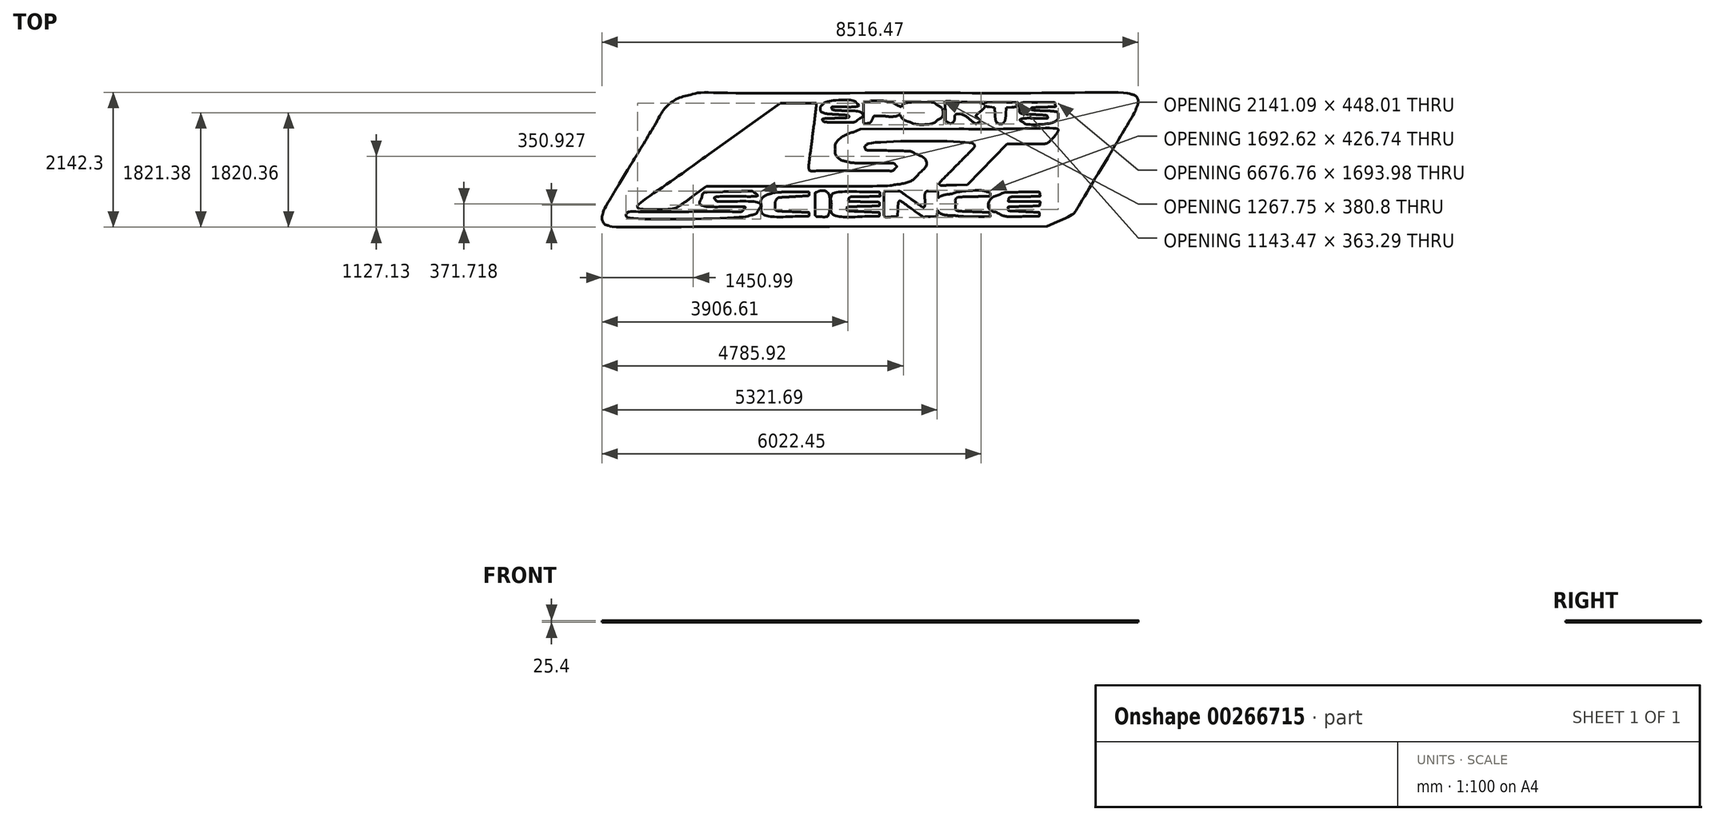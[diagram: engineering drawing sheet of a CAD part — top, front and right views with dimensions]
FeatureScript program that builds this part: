
annotation { "Feature Type Name" : "Feature", "Feature Type Description" : "" }
export const myFeature = defineFeature(function(context is Context, id is Id, definition is map)
    precondition{}
    {
        {
            var Q0;
            Q0=qCreatedBy(makeId("Top.planeOp"),FACE);
            var sketch = newSketch(context, id + "F0", { "sketchPlane" : qUnion([Q0])});
            skFitSpline(sketch, "E0", {"points": [v(-4148.25, -1047.03) * mm, v(-4215.36, -1022.28) * mm, v(-4255.3, -931.26) * mm, v(-4236.55, -845.83) * mm]});
            skFitSpline(sketch, "E1", {"points": [v(-4236.55, -845.83) * mm, v(-4228.8, -810.56) * mm, v(-4052.96, -501.34) * mm, v(-3845.8, -158.69) * mm]});
            skFitSpline(sketch, "E2", {"points": [v(-3845.8, -158.69) * mm, v(-3638.63, 183.97) * mm, v(-3431.5, 527.13) * mm, v(-3385.53, 603.9) * mm]});
            skFitSpline(sketch, "E3", {"points": [v(-3385.53, 603.9) * mm, v(-3262.4, 809.52) * mm, v(-3062.75, 967.71) * mm, v(-2846.13, 1031.34) * mm]});
            skFitSpline(sketch, "E4", {"points": [v(-2846.13, 1031.34) * mm, v(-2747.02, 1060.45) * mm, v(-2388.03, 1063.76) * mm, v(671.28, 1063.76) * mm]});
            skFitSpline(sketch, "E5", {"points": [v(671.28, 1063.76) * mm, v(3028.67, 1063.76) * mm, v(4097.44, 1057.1) * mm, v(4140.4, 1042.12) * mm]});
            skFitSpline(sketch, "E6", {"points": [v(4140.4, 1042.12) * mm, v(4224.04, 1012.96) * mm, v(4260.96, 924.63) * mm, v(4230.7, 826.04) * mm]});
            skFitSpline(sketch, "E7", {"points": [v(4230.7, 826.04) * mm, v(4218.45, 786.14) * mm, v(4013.65, 428.8) * mm, v(3775.57, 31.96) * mm]});
            skFitSpline(sketch, "E8", {"points": [v(3775.57, 31.96) * mm, v(3285.7, -784.61) * mm, v(3221.97, -865.04) * mm, v(2969.12, -985.79) * mm]});
            skFitSpline(sketch, "E9", {"points": [v(-640.01, -1063.28) * mm, v(-2847.05, -1065.57) * mm, v(-4113.85, -1059.7) * mm, v(-4148.25, -1047.03) * mm]});
            skLineSegment(sketch, "E10", {"start": v(2969.12, -985.79) * mm, "end": v(2814.39, -1059.68) * mm});
            skLineSegment(sketch, "E11", {"start": v(2814.39, -1059.68) * mm, "end": v(-640.01, -1063.28) * mm});
            skFitSpline(sketch, "E12", {"points": [v(-1909.68, -885) * mm, v(-1831.18, -868.16) * mm, v(-1800.22, -850.57) * mm, v(-1783.16, -813.12) * mm]});
            skFitSpline(sketch, "E13", {"points": [v(-1783.16, -813.12) * mm, v(-1735.07, -707.58) * mm, v(-1857.4, -664.67) * mm, v(-2208.53, -663.93) * mm]});
            skFitSpline(sketch, "E14", {"points": [v(-2208.53, -663.93) * mm, v(-2337.95, -663.65) * mm, v(-2441.36, -654.67) * mm, v(-2448.52, -643.08) * mm]});
            skFitSpline(sketch, "E15", {"points": [v(-2448.52, -643.08) * mm, v(-2473.2, -603.16) * mm, v(-2350.55, -582.16) * mm, v(-2092.77, -582.16) * mm]});
            skFitSpline(sketch, "E16", {"points": [v(-2092.77, -582.16) * mm, v(-1834, -582.16) * mm, v(-1780.77, -569.44) * mm, v(-1838.6, -521.44) * mm]});
            skFitSpline(sketch, "E17", {"points": [v(-1838.6, -521.44) * mm, v(-1860.25, -503.47) * mm, v(-1961.02, -499.03) * mm, v(-2209.22, -505.1) * mm]});
            skFitSpline(sketch, "E18", {"points": [v(-2209.22, -505.1) * mm, v(-2565.37, -513.82) * mm, v(-2649.73, -532.26) * mm, v(-2673.3, -606.54) * mm]});
            skFitSpline(sketch, "E19", {"points": [v(-2673.3, -606.54) * mm, v(-2703.6, -701.99) * mm, v(-2580.3, -744.45) * mm, v(-2272.36, -744.6) * mm]});
            skFitSpline(sketch, "E20", {"points": [v(-2272.36, -744.6) * mm, v(-2027.25, -744.74) * mm, v(-1977.9, -754.9) * mm, v(-2013.58, -797.9) * mm]});
            skFitSpline(sketch, "E21", {"points": [v(-2013.58, -797.9) * mm, v(-2032.8, -821.05) * mm, v(-2195.36, -826) * mm, v(-2936.17, -826) * mm]});
            skFitSpline(sketch, "E22", {"points": [v(-2936.17, -826) * mm, v(-3663.68, -826) * mm, v(-3839.76, -831.2) * mm, v(-3858.07, -853.27) * mm]});
            skFitSpline(sketch, "E23", {"points": [v(-3858.07, -853.27) * mm, v(-3870.52, -868.27) * mm, v(-3874.69, -886.56) * mm, v(-3867.33, -893.91) * mm]});
            skFitSpline(sketch, "E24", {"points": [v(-3867.33, -893.91) * mm, v(-3843.7, -917.53) * mm, v(-2022.73, -909.24) * mm, v(-1909.68, -885) * mm]});
            skFitSpline(sketch, "E25", {"points": [v(-965.13, -866.64) * mm, v(-965.13, -841.88) * mm, v(-1009.38, -834.25) * mm, v(-1200.82, -826) * mm]});
            skFitSpline(sketch, "E26", {"points": [v(-1200.82, -826) * mm, v(-1452.9, -815.13) * mm, v(-1503.61, -796.24) * mm, v(-1503.61, -713.2) * mm]});
            skFitSpline(sketch, "E27", {"points": [v(-1503.61, -713.2) * mm, v(-1503.61, -670.41) * mm, v(-1459.61, -606.2) * mm, v(-1425.96, -599.9) * mm]});
            skFitSpline(sketch, "E28", {"points": [v(-1425.96, -599.9) * mm, v(-1418.38, -598.47) * mm, v(-1311.6, -591.62) * mm, v(-1188.65, -584.66) * mm]});
            skFitSpline(sketch, "E29", {"points": [v(-1188.65, -584.66) * mm, v(-1009.14, -574.5) * mm, v(-965.13, -566) * mm, v(-965.13, -541.52) * mm]});
            skFitSpline(sketch, "E30", {"points": [v(-965.13, -541.52) * mm, v(-965.13, -515.92) * mm, v(-1007.44, -511.26) * mm, v(-1229.3, -512.38) * mm]});
            skFitSpline(sketch, "E31", {"points": [v(-1229.3, -512.38) * mm, v(-1378.73, -513.14) * mm, v(-1525.25, -524.43) * mm, v(-1566.67, -538.37) * mm]});
            skFitSpline(sketch, "E32", {"points": [v(-1566.67, -538.37) * mm, v(-1673.12, -574.21) * mm, v(-1731.48, -644.13) * mm, v(-1723.5, -726.27) * mm]});
            skFitSpline(sketch, "E33", {"points": [v(-1723.5, -726.27) * mm, v(-1711.16, -853.4) * mm, v(-1551.25, -905.43) * mm, v(-1188.65, -900.29) * mm]});
            skFitSpline(sketch, "E34", {"points": [v(-1188.65, -900.29) * mm, v(-1004.92, -897.68) * mm, v(-965.13, -891.7) * mm, v(-965.13, -866.64) * mm]});
            skFitSpline(sketch, "E35", {"points": [v(-662.5, -875.14) * mm, v(-640.03, -816.56) * mm, v(-649.19, -550.64) * mm, v(-674.56, -525.27) * mm]});
            skFitSpline(sketch, "E36", {"points": [v(-674.56, -525.27) * mm, v(-700.59, -499.24) * mm, v(-788.58, -492.89) * mm, v(-841.55, -513.22) * mm]});
            skFitSpline(sketch, "E37", {"points": [v(-841.55, -513.22) * mm, v(-867.46, -523.16) * mm, v(-873.7, -559.92) * mm, v(-873.7, -702.87) * mm]});
            skFitSpline(sketch, "E38", {"points": [v(-873.7, -702.87) * mm, v(-873.7, -800.4) * mm, v(-867.6, -886.28) * mm, v(-860.15, -893.73) * mm]});
            skFitSpline(sketch, "E39", {"points": [v(-860.15, -893.73) * mm, v(-852.7, -901.19) * mm, v(-807.96, -907.28) * mm, v(-760.72, -907.28) * mm]});
            skFitSpline(sketch, "E40", {"points": [v(-760.72, -907.28) * mm, v(-701.16, -907.28) * mm, v(-671.06, -897.43) * mm, v(-662.5, -875.14) * mm]});
            skFitSpline(sketch, "E41", {"points": [v(152.47, -866.64) * mm, v(152.47, -841.9) * mm, v(108.44, -834.25) * mm, v(-81.21, -826) * mm]});
            skFitSpline(sketch, "E42", {"points": [v(-81.21, -826) * mm, v(-307.16, -816.18) * mm, v(-365.7, -803.51) * mm, v(-365.7, -764.45) * mm]});
            skFitSpline(sketch, "E43", {"points": [v(-365.7, -764.45) * mm, v(-365.7, -754.27) * mm, v(-249.1, -743.38) * mm, v(-106.61, -740.25) * mm]});
            skFitSpline(sketch, "E44", {"points": [v(-106.61, -740.25) * mm, v(107.6, -735.55) * mm, v(152.47, -729.28) * mm, v(152.47, -704.08) * mm]});
            skFitSpline(sketch, "E45", {"points": [v(152.47, -704.08) * mm, v(152.47, -678.95) * mm, v(108.56, -672.6) * mm, v(-97.94, -667.88) * mm]});
            skFitSpline(sketch, "E46", {"points": [v(-97.94, -667.88) * mm, v(-280.57, -663.71) * mm, v(-346.15, -655.62) * mm, v(-340.27, -637.96) * mm]});
            skFitSpline(sketch, "E47", {"points": [v(-340.27, -637.96) * mm, v(-327.63, -600.06) * mm, v(-249.7, -586.38) * mm, v(-34, -584.19) * mm]});
            skFitSpline(sketch, "E48", {"points": [v(-34, -584.19) * mm, v(144.6, -582.37) * mm, v(164.88, -578.42) * mm, v(158.68, -546.6) * mm]});
            skFitSpline(sketch, "E49", {"points": [v(158.68, -546.6) * mm, v(152.56, -515.2) * mm, v(124.48, -511.05) * mm, v(-81.57, -511.1) * mm]});
            skFitSpline(sketch, "E50", {"points": [v(-81.57, -511.1) * mm, v(-484.03, -511.2) * mm, v(-609.53, -558.93) * mm, v(-609.53, -711.89) * mm]});
            skFitSpline(sketch, "E51", {"points": [v(-609.53, -711.89) * mm, v(-609.53, -850.23) * mm, v(-454.7, -905.46) * mm, v(-81.21, -900.33) * mm]});
            skFitSpline(sketch, "E52", {"points": [v(-81.21, -900.33) * mm, v(111.53, -897.68) * mm, v(152.47, -891.78) * mm, v(152.47, -866.64) * mm]});
            skFitSpline(sketch, "E53", {"points": [v(443.19, -785.36) * mm, v(446.62, -723.9) * mm, v(455.77, -667.35) * mm, v(463.5, -659.7) * mm]});
            skFitSpline(sketch, "E54", {"points": [v(463.5, -659.7) * mm, v(471.25, -652.06) * mm, v(559.88, -704.89) * mm, v(660.47, -777.1) * mm]});
            skFitSpline(sketch, "E55", {"points": [v(660.47, -777.1) * mm, v(838, -904.56) * mm, v(846.6, -908.23) * mm, v(955.1, -902.76) * mm]});
            skFitSpline(sketch, "E56", {"points": [v(1072.79, -715.96) * mm, v(1079.15, -521.13) * mm, v(1070.28, -501.77) * mm, v(974.4, -501.2) * mm]});
            skFitSpline(sketch, "E57", {"points": [v(974.4, -501.2) * mm, v(899.17, -500.74) * mm, v(873.83, -537.22) * mm, v(873.83, -645.99) * mm]});
            skFitSpline(sketch, "E58", {"points": [v(873.83, -645.99) * mm, v(873.83, -698.97) * mm, v(866.97, -746.44) * mm, v(858.59, -751.48) * mm]});
            skFitSpline(sketch, "E59", {"points": [v(858.59, -751.48) * mm, v(850.2, -756.51) * mm, v(761.96, -702.19) * mm, v(662.48, -630.76) * mm]});
            skFitSpline(sketch, "E60", {"points": [v(662.48, -630.76) * mm, v(494.48, -510.12) * mm, v(473.93, -500.88) * mm, v(373.63, -500.88) * mm]});
            skFitSpline(sketch, "E61", {"points": [v(373.63, -500.88) * mm, v(240.2, -500.88) * mm, v(223.59, -525.03) * mm, v(223.59, -719) * mm]});
            skFitSpline(sketch, "E62", {"points": [v(223.59, -719) * mm, v(223.59, -883.72) * mm, v(243.43, -911.4) * mm, v(355.57, -903.13) * mm]});
            skLineSegment(sketch, "E63", {"start": v(955.1, -902.76) * mm, "end": v(1066.87, -897.12) * mm});
            skLineSegment(sketch, "E64", {"start": v(1066.87, -897.12) * mm, "end": v(1072.79, -715.96) * mm});
            skFitSpline(sketch, "E65", {"points": [v(1906.34, -871.72) * mm, v(1900.48, -841.01) * mm, v(1867.43, -834.78) * mm, v(1664.02, -826) * mm]});
            skFitSpline(sketch, "E66", {"points": [v(1664.02, -826) * mm, v(1413.33, -815.19) * mm, v(1361.5, -796.16) * mm, v(1361.5, -714.9) * mm]});
            skFitSpline(sketch, "E67", {"points": [v(1361.5, -714.9) * mm, v(1361.5, -620.03) * mm, v(1427.27, -593.1) * mm, v(1678.51, -585.13) * mm]});
            skFitSpline(sketch, "E68", {"points": [v(1678.51, -585.13) * mm, v(1857.77, -579.44) * mm, v(1910.15, -571.47) * mm, v(1910.15, -549.88) * mm]});
            skFitSpline(sketch, "E69", {"points": [v(1910.15, -549.88) * mm, v(1910.15, -534.53) * mm, v(1886.04, -515.93) * mm, v(1856.58, -508.53) * mm]});
            skFitSpline(sketch, "E70", {"points": [v(1856.58, -508.53) * mm, v(1780.6, -489.46) * mm, v(1385.44, -514.03) * mm, v(1300.55, -543.11) * mm]});
            skFitSpline(sketch, "E71", {"points": [v(1300.55, -543.11) * mm, v(1068.4, -622.62) * mm, v(1090.71, -831.15) * mm, v(1336.85, -882.5) * mm]});
            skFitSpline(sketch, "E72", {"points": [v(1336.85, -882.5) * mm, v(1389.53, -893.49) * mm, v(1540.74, -903.56) * mm, v(1672.88, -904.88) * mm]});
            skFitSpline(sketch, "E73", {"points": [v(1672.88, -904.88) * mm, v(1891.44, -907.06) * mm, v(1912.51, -904.07) * mm, v(1906.34, -871.72) * mm]});
            skLineSegment(sketch, "E74", {"start": v(355.57, -903.13) * mm, "end": v(436.95, -897.12) * mm});
            skLineSegment(sketch, "E75", {"start": v(436.95, -897.12) * mm, "end": v(443.19, -785.36) * mm});
            skFitSpline(sketch, "E76", {"points": [v(2692.47, -866.64) * mm, v(2692.47, -841.93) * mm, v(2646.28, -833.8) * mm, v(2448.63, -823.68) * mm]});
            skFitSpline(sketch, "E77", {"points": [v(2448.63, -823.68) * mm, v(2314.51, -816.8) * mm, v(2202.5, -809.95) * mm, v(2199.7, -808.44) * mm]});
            skFitSpline(sketch, "E78", {"points": [v(2199.7, -808.44) * mm, v(2196.91, -806.92) * mm, v(2194.63, -792.25) * mm, v(2194.63, -775.83) * mm]});
            skFitSpline(sketch, "E79", {"points": [v(2194.63, -775.83) * mm, v(2194.63, -751.5) * mm, v(2240.7, -744.91) * mm, v(2443.3, -740.27) * mm]});
            skFitSpline(sketch, "E80", {"points": [v(2443.3, -740.27) * mm, v(2661.31, -735.26) * mm, v(2692.81, -730.18) * mm, v(2698.79, -699) * mm]});
            skFitSpline(sketch, "E81", {"points": [v(2698.79, -699) * mm, v(2705, -666.65) * mm, v(2682.4, -663.44) * mm, v(2448.42, -663.44) * mm]});
            skFitSpline(sketch, "E82", {"points": [v(2448.42, -663.44) * mm, v(2251.72, -663.44) * mm, v(2193.23, -657.47) * mm, v(2199.69, -638.04) * mm]});
            skFitSpline(sketch, "E83", {"points": [v(2199.69, -638.04) * mm, v(2211.68, -601.99) * mm, v(2298.44, -587.33) * mm, v(2516.16, -584.57) * mm]});
            skFitSpline(sketch, "E84", {"points": [v(2516.16, -584.57) * mm, v(2685.03, -582.42) * mm, v(2704.84, -578.3) * mm, v(2698.52, -546.6) * mm]});
            skFitSpline(sketch, "E85", {"points": [v(2698.52, -546.6) * mm, v(2692.16, -514.66) * mm, v(2663.21, -511.3) * mm, v(2414.27, -513.63) * mm]});
            skFitSpline(sketch, "E86", {"points": [v(2414.27, -513.63) * mm, v(2188.21, -515.74) * mm, v(2122.77, -523.24) * mm, v(2059.46, -554.27) * mm]});
            skFitSpline(sketch, "E87", {"points": [v(2059.46, -554.27) * mm, v(1914.7, -625.23) * mm, v(1889.49, -772.94) * mm, v(2011.38, -835.97) * mm]});
            skFitSpline(sketch, "E88", {"points": [v(2011.38, -835.97) * mm, v(2114.14, -889.1) * mm, v(2216.94, -903.93) * mm, v(2458.79, -900.47) * mm]});
            skFitSpline(sketch, "E89", {"points": [v(2458.79, -900.47) * mm, v(2651.47, -897.7) * mm, v(2692.47, -891.77) * mm, v(2692.47, -866.64) * mm]});
            skFitSpline(sketch, "E90", {"points": [v(-3044.84, -743.07) * mm, v(-3022.26, -730.98) * mm, v(-2911.72, -653.26) * mm, v(-2799.19, -570.35) * mm]});
            skFitSpline(sketch, "E91", {"points": [v(-1170.26, -419.45) * mm, v(-278.51, -419.35) * mm, v(302.95, -411.36) * mm, v(384.81, -398.08) * mm]});
            skFitSpline(sketch, "E92", {"points": [v(384.81, -398.08) * mm, v(564.97, -368.85) * mm, v(697.9, -307.25) * mm, v(782.22, -213.91) * mm]});
            skFitSpline(sketch, "E93", {"points": [v(782.22, -213.91) * mm, v(894.41, -89.72) * mm, v(875.35, 13.96) * mm, v(725.83, 92.8) * mm]});
            skFitSpline(sketch, "E94", {"points": [v(725.83, 92.8) * mm, v(648.95, 133.34) * mm, v(603.99, 138.78) * mm, v(288.2, 145.7) * mm]});
            skFitSpline(sketch, "E95", {"points": [v(288.2, 145.7) * mm, v(-1, 152.06) * mm, v(-65.82, 158.87) * mm, v(-75.43, 183.93) * mm]});
            skFitSpline(sketch, "E96", {"points": [v(-75.43, 183.93) * mm, v(-81.87, 200.7) * mm, v(-74.37, 222.5) * mm, v(-58.78, 232.38) * mm]});
            skFitSpline(sketch, "E97", {"points": [v(-58.78, 232.38) * mm, v(-16.34, 259.25) * mm, v(1640.34, 256.2) * mm, v(1657.02, 229.23) * mm]});
            skFitSpline(sketch, "E98", {"points": [v(1657.02, 229.23) * mm, v(1664.42, 217.25) * mm, v(1540.14, 76.05) * mm, v(1380.12, -85.34) * mm]});
            skFitSpline(sketch, "E99", {"points": [v(1380.12, -85.34) * mm, v(1220.43, -246.4) * mm, v(1094.94, -383.33) * mm, v(1101.25, -389.64) * mm]});
            skFitSpline(sketch, "E100", {"points": [v(1101.25, -389.64) * mm, v(1116.35, -404.74) * mm, v(1173.8, -407.5) * mm, v(1380.1, -403) * mm]});
            skLineSegment(sketch, "E101", {"start": v(-2799.19, -570.35) * mm, "end": v(-2594.6, -419.6) * mm});
            skLineSegment(sketch, "E102", {"start": v(-2594.6, -419.6) * mm, "end": v(-1170.26, -419.45) * mm});
            skFitSpline(sketch, "E103", {"points": [v(2487.08, 251.27) * mm, v(2655.92, 251.44) * mm, v(2804.4, 258.3) * mm, v(2817.05, 266.5) * mm]});
            skFitSpline(sketch, "E104", {"points": [v(2817.05, 266.5) * mm, v(2853.03, 289.88) * mm, v(2987.1, 455.84) * mm, v(2987.1, 477) * mm]});
            skFitSpline(sketch, "E105", {"points": [v(2987.1, 477) * mm, v(2987.1, 488.67) * mm, v(2381.53, 493.8) * mm, v(1417.39, 490.32) * mm]});
            skLineSegment(sketch, "E106", {"start": v(1380.1, -403) * mm, "end": v(1551.09, -399.28) * mm});
            skLineSegment(sketch, "E107", {"start": v(1551.09, -399.28) * mm, "end": v(1865.6, -74.16) * mm});
            skLineSegment(sketch, "E108", {"start": v(1865.6, -74.16) * mm, "end": v(2180.1, 250.96) * mm});
            skLineSegment(sketch, "E109", {"start": v(2180.1, 250.96) * mm, "end": v(2487.08, 251.27) * mm});
            skFitSpline(sketch, "E110", {"points": [v(-267.64, 438.03) * mm, v(-419.47, 376.66) * mm, v(-548.57, 252.64) * mm, v(-548.57, 168.14) * mm]});
            skFitSpline(sketch, "E111", {"points": [v(-548.57, 168.14) * mm, v(-548.57, 87.89) * mm, v(-461.22, -1.7) * mm, v(-353.93, -31.5) * mm]});
            skFitSpline(sketch, "E112", {"points": [v(-353.93, -31.5) * mm, v(-310.1, -43.66) * mm, v(-126.78, -53.67) * mm, v(53.46, -53.73) * mm]});
            skFitSpline(sketch, "E113", {"points": [v(53.46, -53.73) * mm, v(308.8, -53.82) * mm, v(386.36, -60.1) * mm, v(404.68, -82.17) * mm]});
            skFitSpline(sketch, "E114", {"points": [v(404.68, -82.17) * mm, v(422.83, -104.04) * mm, v(420.75, -117.93) * mm, v(395.56, -143.13) * mm]});
            skFitSpline(sketch, "E115", {"points": [v(395.56, -143.13) * mm, v(366.93, -171.75) * mm, v(281.88, -175.76) * mm, v(-296.66, -175.76) * mm]});
            skFitSpline(sketch, "E116", {"points": [v(-296.66, -175.76) * mm, v(-833.66, -175.76) * mm, v(-958.22, -170.63) * mm, v(-966.84, -148.16) * mm]});
            skFitSpline(sketch, "E117", {"points": [v(-966.84, -148.16) * mm, v(-972.67, -132.98) * mm, v(-949.52, 93.14) * mm, v(-915.4, 354.32) * mm]});
            skFitSpline(sketch, "E118", {"points": [v(-915.4, 354.32) * mm, v(-881.29, 615.5) * mm, v(-853.37, 845.4) * mm, v(-853.37, 865.2) * mm]});
            skFitSpline(sketch, "E119", {"points": [v(-853.37, 865.2) * mm, v(-853.37, 897.93) * mm, v(-879.12, 901.2) * mm, v(-1137.02, 901.2) * mm]});
            skLineSegment(sketch, "E120", {"start": v(1417.39, 490.32) * mm, "end": v(-152.33, 484.64) * mm});
            skLineSegment(sketch, "E121", {"start": v(-152.33, 484.64) * mm, "end": v(-267.64, 438.03) * mm});
            skFitSpline(sketch, "E122", {"points": [v(-2559.89, 87.22) * mm, v(-3186.46, -360.48) * mm, v(-3693.79, -735.38) * mm, v(-3687.28, -745.9) * mm]});
            skFitSpline(sketch, "E123", {"points": [v(-3687.28, -745.9) * mm, v(-3670.65, -772.82) * mm, v(-3095.7, -770.28) * mm, v(-3044.84, -743.07) * mm]});
            skLineSegment(sketch, "E124", {"start": v(-1137.02, 901.2) * mm, "end": v(-1420.67, 901.2) * mm});
            skLineSegment(sketch, "E125", {"start": v(-1420.67, 901.2) * mm, "end": v(-2559.89, 87.22) * mm});
            skFitSpline(sketch, "E126", {"points": [v(-2170.95, -137.61) * mm, v(-2162.83, -115.59) * mm, v(-1419.44, 432.87) * mm, v(-1396.93, 433.45) * mm]});
            skFitSpline(sketch, "E127", {"points": [v(-1396.93, 433.45) * mm, v(-1371.02, 434.11) * mm, v(-1381.92, 311.36) * mm, v(-1428.49, 78.24) * mm]});
            skFitSpline(sketch, "E128", {"points": [v(-1825.51, -150.85) * mm, v(-2035.43, -154.17) * mm, v(-2175.08, -148.81) * mm, v(-2170.95, -137.61) * mm]});
            skLineSegment(sketch, "E129", {"start": v(-1428.49, 78.24) * mm, "end": v(-1473.13, -145.28) * mm});
            skLineSegment(sketch, "E130", {"start": v(-1473.13, -145.28) * mm, "end": v(-1825.51, -150.85) * mm});
            skFitSpline(sketch, "E131", {"points": [v(36.58, 642.37) * mm, v(61.88, 695.15) * mm, v(70.51, 698) * mm, v(205.38, 698) * mm]});
            skFitSpline(sketch, "E132", {"points": [v(205.38, 698) * mm, v(433.48, 698) * mm, v(543.67, 789.35) * mm, v(416.27, 872.82) * mm]});
            skFitSpline(sketch, "E133", {"points": [v(416.27, 872.82) * mm, v(360.56, 909.32) * mm, v(44.54, 937.09) * mm, v(-48.74, 913.68) * mm]});
            skFitSpline(sketch, "E134", {"points": [v(-48.74, 913.68) * mm, v(-99.63, 900.9) * mm, v(-101.53, 895.02) * mm, v(-101.53, 750.1) * mm]});
            skFitSpline(sketch, "E135", {"points": [v(-101.53, 750.1) * mm, v(-101.53, 598.82) * mm, v(-89.4, 573.77) * mm, v(-20.4, 582.78) * mm]});
            skFitSpline(sketch, "E136", {"points": [v(-20.4, 582.78) * mm, v(-3.73, 584.95) * mm, v(21.91, 611.77) * mm, v(36.58, 642.37) * mm]});
            skFitSpline(sketch, "E137", {"points": [v(45.79, 804.68) * mm, v(51.15, 820.77) * mm, v(93.99, 830.08) * mm, v(162.63, 830.08) * mm]});
            skFitSpline(sketch, "E138", {"points": [v(162.63, 830.08) * mm, v(231.26, 830.08) * mm, v(274.1, 820.77) * mm, v(279.47, 804.68) * mm]});
            skFitSpline(sketch, "E139", {"points": [v(279.47, 804.68) * mm, v(285.63, 786.19) * mm, v(253.84, 779.28) * mm, v(162.63, 779.28) * mm]});
            skFitSpline(sketch, "E140", {"points": [v(162.63, 779.28) * mm, v(71.41, 779.28) * mm, v(39.62, 786.19) * mm, v(45.79, 804.68) * mm]});
            skFitSpline(sketch, "E141", {"points": [v(1074.96, 632.44) * mm, v(1151.95, 689.92) * mm, v(1149.67, 809.38) * mm, v(1070.46, 868.53) * mm]});
            skFitSpline(sketch, "E142", {"points": [v(1070.46, 868.53) * mm, v(1021.83, 904.83) * mm, v(984.65, 911.35) * mm, v(826.62, 911.28) * mm]});
            skFitSpline(sketch, "E143", {"points": [v(826.62, 911.28) * mm, v(614.06, 911.2) * mm, v(517.58, 875.06) * mm, v(495.55, 787.3) * mm]});
            skFitSpline(sketch, "E144", {"points": [v(495.55, 787.3) * mm, v(478.41, 719) * mm, v(539.72, 635.37) * mm, v(631.89, 601.3) * mm]});
            skFitSpline(sketch, "E145", {"points": [v(631.89, 601.3) * mm, v(735.24, 563.08) * mm, v(1007.73, 582.24) * mm, v(1074.96, 632.44) * mm]});
            skFitSpline(sketch, "E146", {"points": [v(682.24, 689.3) * mm, v(609.88, 761.65) * mm, v(684.77, 840.24) * mm, v(826.1, 840.24) * mm]});
            skFitSpline(sketch, "E147", {"points": [v(826.1, 840.24) * mm, v(956.76, 840.24) * mm, v(1031.93, 729.67) * mm, v(936.12, 678.4) * mm]});
            skFitSpline(sketch, "E148", {"points": [v(936.12, 678.4) * mm, v(875.38, 645.88) * mm, v(718.93, 652.6) * mm, v(682.24, 689.3) * mm]});
            skFitSpline(sketch, "E149", {"points": [v(1313.44, 591.63) * mm, v(1326.11, 599.84) * mm, v(1339.9, 624.85) * mm, v(1344.08, 647.2) * mm]});
            skFitSpline(sketch, "E150", {"points": [v(1344.08, 647.2) * mm, v(1357.22, 717.46) * mm, v(1483.73, 712.75) * mm, v(1586.67, 638.18) * mm]});
            skFitSpline(sketch, "E151", {"points": [v(1586.67, 638.18) * mm, v(1681.45, 569.52) * mm, v(1684.14, 568.7) * mm, v(1726.46, 595.47) * mm]});
            skFitSpline(sketch, "E152", {"points": [v(1726.46, 595.47) * mm, v(1751.84, 611.52) * mm, v(1750.62, 620.32) * mm, v(1718.04, 656.33) * mm]});
            skFitSpline(sketch, "E153", {"points": [v(1718.04, 656.33) * mm, v(1680.7, 697.58) * mm, v(1680.82, 699.36) * mm, v(1723.92, 745.24) * mm]});
            skFitSpline(sketch, "E154", {"points": [v(1723.92, 745.24) * mm, v(1828.43, 856.49) * mm, v(1757.06, 904.6) * mm, v(1468.39, 917.52) * mm]});
            skFitSpline(sketch, "E155", {"points": [v(1468.39, 917.52) * mm, v(1210.11, 929.07) * mm, v(1198.95, 922.02) * mm, v(1198.95, 747.32) * mm]});
            skFitSpline(sketch, "E156", {"points": [v(1198.95, 747.32) * mm, v(1198.95, 646.3) * mm, v(1206.57, 614.3) * mm, v(1234.5, 598.03) * mm]});
            skFitSpline(sketch, "E157", {"points": [v(1234.5, 598.03) * mm, v(1277.42, 573.03) * mm, v(1283.9, 572.5) * mm, v(1313.44, 591.63) * mm]});
            skFitSpline(sketch, "E158", {"points": [v(1372.2, 798.74) * mm, v(1364.9, 810.55) * mm, v(1372.18, 825.3) * mm, v(1388.37, 831.5) * mm]});
            skFitSpline(sketch, "E159", {"points": [v(1388.37, 831.5) * mm, v(1434.58, 849.23) * mm, v(1595.19, 832.35) * mm, v(1595.19, 809.76) * mm]});
            skFitSpline(sketch, "E160", {"points": [v(1595.19, 809.76) * mm, v(1595.19, 782) * mm, v(1388.84, 771.82) * mm, v(1372.2, 798.74) * mm]});
            skFitSpline(sketch, "E161", {"points": [v(2129.88, 602) * mm, v(2141.7, 616.25) * mm, v(2154.26, 673.4) * mm, v(2157.77, 729) * mm]});
            skFitSpline(sketch, "E162", {"points": [v(2251.76, 836.39) * mm, v(2321.23, 841.4) * mm, v(2338, 849.8) * mm, v(2332.76, 877.03) * mm]});
            skFitSpline(sketch, "E163", {"points": [v(2332.76, 877.03) * mm, v(2326.98, 907.07) * mm, v(2294.45, 911.36) * mm, v(2072.43, 911.36) * mm]});
            skFitSpline(sketch, "E164", {"points": [v(2072.43, 911.36) * mm, v(1860.44, 911.36) * mm, v(1818.7, 906.34) * mm, v(1818.7, 880.88) * mm]});
            skFitSpline(sketch, "E165", {"points": [v(1818.7, 880.88) * mm, v(1818.7, 860.56) * mm, v(1845.8, 847.01) * mm, v(1899.99, 840.24) * mm]});
            skLineSegment(sketch, "E166", {"start": v(2157.77, 729) * mm, "end": v(2164.15, 830.08) * mm});
            skLineSegment(sketch, "E167", {"start": v(2164.15, 830.08) * mm, "end": v(2251.76, 836.39) * mm});
            skFitSpline(sketch, "E168", {"points": [v(1987.57, 718.76) * mm, v(1991.03, 657.54) * mm, v(2004.75, 600.53) * mm, v(2018.05, 592.07) * mm]});
            skFitSpline(sketch, "E169", {"points": [v(2018.05, 592.07) * mm, v(2054.93, 568.62) * mm, v(2105.94, 573.15) * mm, v(2129.88, 602) * mm]});
            skLineSegment(sketch, "E170", {"start": v(1899.99, 840.24) * mm, "end": v(1981.27, 830.08) * mm});
            skLineSegment(sketch, "E171", {"start": v(1981.27, 830.08) * mm, "end": v(1987.57, 718.76) * mm});
            skFitSpline(sketch, "E172", {"points": [v(2942.92, 614.82) * mm, v(2967.22, 627.83) * mm, v(2987.1, 655.32) * mm, v(2987.1, 675.9) * mm]});
            skFitSpline(sketch, "E173", {"points": [v(2987.1, 675.9) * mm, v(2987.1, 743.64) * mm, v(2927.14, 768.72) * mm, v(2740, 779.28) * mm]});
            skFitSpline(sketch, "E174", {"points": [v(2740, 779.28) * mm, v(2640.05, 784.92) * mm, v(2559.92, 798.48) * mm, v(2560.02, 809.76) * mm]});
            skFitSpline(sketch, "E175", {"points": [v(2560.02, 809.76) * mm, v(2560.12, 821.47) * mm, v(2642.59, 832.55) * mm, v(2754.67, 835.91) * mm]});
            skFitSpline(sketch, "E176", {"points": [v(2754.67, 835.91) * mm, v(2925.68, 841.04) * mm, v(2948.33, 845.95) * mm, v(2942.28, 876.55) * mm]});
            skFitSpline(sketch, "E177", {"points": [v(2942.28, 876.55) * mm, v(2936.25, 907.06) * mm, v(2906.6, 911.24) * mm, v(2702.17, 910.41) * mm]});
            skFitSpline(sketch, "E178", {"points": [v(2702.17, 910.41) * mm, v(2455.97, 909.41) * mm, v(2377.5, 887.97) * mm, v(2377.5, 821.7) * mm]});
            skFitSpline(sketch, "E179", {"points": [v(2377.5, 821.7) * mm, v(2377.5, 753.59) * mm, v(2437.36, 728.87) * mm, v(2627.82, 718.32) * mm]});
            skFitSpline(sketch, "E180", {"points": [v(2627.82, 718.32) * mm, v(2748.8, 711.61) * mm, v(2814.02, 699.52) * mm, v(2819.55, 682.76) * mm]});
            skFitSpline(sketch, "E181", {"points": [v(2819.55, 682.76) * mm, v(2825.86, 663.63) * mm, v(2780.15, 657.36) * mm, v(2634.4, 657.36) * mm]});
            skFitSpline(sketch, "E182", {"points": [v(2634.4, 657.36) * mm, v(2444.35, 657.36) * mm, v(2378.94, 635.57) * mm, v(2440.94, 592.91) * mm]});
            skFitSpline(sketch, "E183", {"points": [v(2440.94, 592.91) * mm, v(2478.46, 567.1) * mm, v(2887.09, 584.94) * mm, v(2942.92, 614.82) * mm]});
            skFitSpline(sketch, "E184", {"points": [v(-199.65, 630.03) * mm, v(-106.12, 714.68) * mm, v(-179.95, 766.38) * mm, v(-412.8, 779.28) * mm]});
            skFitSpline(sketch, "E185", {"points": [v(-412.8, 779.28) * mm, v(-533.8, 785.98) * mm, v(-599, 798.08) * mm, v(-604.54, 814.84) * mm]});
            skFitSpline(sketch, "E186", {"points": [v(-604.54, 814.84) * mm, v(-610.82, 833.86) * mm, v(-567.84, 840.32) * mm, v(-433.43, 840.55) * mm]});
            skFitSpline(sketch, "E187", {"points": [v(-433.43, 840.55) * mm, v(-243.91, 840.88) * mm, v(-174.91, 860.79) * mm, v(-217.1, 902.97) * mm]});
            skFitSpline(sketch, "E188", {"points": [v(-217.1, 902.97) * mm, v(-250.39, 936.26) * mm, v(-696.19, 918.58) * mm, v(-740, 882.23) * mm]});
            skFitSpline(sketch, "E189", {"points": [v(-740, 882.23) * mm, v(-782.86, 846.65) * mm, v(-780.83, 767.34) * mm, v(-736.53, 746.89) * mm]});
            skFitSpline(sketch, "E190", {"points": [v(-736.53, 746.89) * mm, v(-716.98, 737.86) * mm, v(-618.68, 725.45) * mm, v(-518.1, 719.32) * mm]});
            skFitSpline(sketch, "E191", {"points": [v(-518.1, 719.32) * mm, v(-417.16, 713.16) * mm, v(-335.21, 699.05) * mm, v(-335.21, 687.84) * mm]});
            skFitSpline(sketch, "E192", {"points": [v(-335.21, 687.84) * mm, v(-335.21, 676.41) * mm, v(-406.36, 665.28) * mm, v(-497.77, 662.4) * mm]});
            skFitSpline(sketch, "E193", {"points": [v(-497.77, 662.4) * mm, v(-689.05, 656.38) * mm, v(-758.02, 643.27) * mm, v(-741.25, 616.12) * mm]});
            skFitSpline(sketch, "E194", {"points": [v(-741.25, 616.12) * mm, v(-734.45, 605.13) * mm, v(-620.14, 596.4) * mm, v(-482.93, 596.4) * mm]});
            skFitSpline(sketch, "E195", {"points": [v(-482.93, 596.4) * mm, v(-282.43, 596.4) * mm, v(-229.93, 602.63) * mm, v(-199.65, 630.03) * mm]});
            skSolve(sketch);
        }
        {
            var Q0;
            Q0 = qSketchRegion(id + "F0", true);
            extrude(context, id + "F1", {"entities" : qUnion([Q0]), "depth" : 25.4 * mm});
        }
    });
